# Revit family: Plumbing-Flushometer-Sloan-Valve-ROYAL-152 ESS_
name_source: partatom
category: Plumbing Fixtures
units: mm (PartAtom-declared; Revit-internal decimal feet)

## family parameters
Cut with Voids When Loaded = Yes
Host = Face
OmniClass Number = 23.45.05.14.99
OmniClass Title = Other Sanitary Washing Plumbing Fixtures
Part Type = Normal
Room Calculation Point = No
Round Connector Dimension = Use Diameter
Shared = No

## types (1)
- Not a Type - Load Type Catalog!
    11-12 3/4 = No
    13-14 3/4 = No
    15 3/4 = No
    18 3/4 = No
    19 3/4 = No
    2 3/4 = Yes
    2-10 3/4 = No
    7-8 3/4 = No
    Apparent Load = 0 VA
    Assembly Code = D2020300
    CW Connection = Yes
    CWFU = 0
    Centerline of Supply from Top of Fixture = 14 1/2"
    Centerline of Supply to Centerline of Valve = 4 3/4"
    Connector Description = Electrical Connection
    Current = 0 A
    Default Elevation = 0"
    Description = 1.6 gpf, XL Sweat Solder Adapter Kit, Rough Brass Finish, Less Flush Connection, Fixture Connection Rear Spud, Single Flush, Electrical Override, Hardwired, Sensor-Operated, Royal® Concealed Sensor Hardwired Water Closet Flushometer.
    Edition number = 1
    Flush Rate = 1.6 gpf (6.0 Lpf)
    Flushometer Material = Sloan Valve - Finish - Rough Brass
    HW Connection = No
    HWFU = 0
    Keynote = 15410
    Manufacturer = Sloan Valve
    Model = Model not specified - Load type catalog!
    Number of Poles = 1
    Operating Water Pressure = 15 – 80 PSI (103 – 552 kPa)
    Part Number = 3451605
    Power Factor = 1
    Product Material = Sloan Valve - Finish - Rough Brass
    Product data url = https://bimobject.com
    URL = www.sloanvalve.com
    Valve Pressure Drop = 0.00 psi
    Vent Connection = No
    Voltage = 24 V
    WFU = 0
    Waste Connection = No
    Water Inlet Connection Description = Water Inlet Connection
    Water Inlet Connection Diameter = 1"
    z_Box Height = 12"
    z_Box Void Offset = 5"
    z_Box Width = 12"
    z_Button = No
    z_Connector Offset = 8 9/16"
    z_Sensor Plate EL-1500 = Yes
    z_Sensor Plate EL-461 = No
    z_Valve Actuator = No
    z_Wall Box = No
    z_Wall Box Small = No

## geometry (parser evidence)
native form markers: Sweep x1
no freeform markers — native parametric forms only
